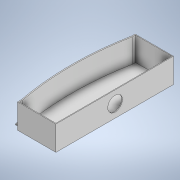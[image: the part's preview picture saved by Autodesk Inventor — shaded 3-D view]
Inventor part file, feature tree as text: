
AUTODESK INVENTOR PART (.ipt)
format: ipt  version: 2020.2 (Build 242310000, 310)  size: 199,680 bytes
history: native  units: mm
features: extrude x9, sketch x9
ambient origin geometry x8: Origin, YZ Plane, XZ Plane, XY Plane, X Axis, Y Axis, Z Axis, Center Point
bodies: Solide1 (feature_tree)
feature tree (18):
  extrude  "Extrusion1"  Depth=301.169mm
  extrude  "Extrusion2"  Depth=65.0mm TaperAngle=0.0deg
  extrude  "Extrusion3"  Depth=10.0mm TaperAngle=0.0deg
  extrude  "Extrusion4"  Depth=10.0mm TaperAngle=0.0deg
  extrude  "Extrusion5"  Depth=2.0mm
  extrude  "Extrusion6"  Depth=2.0mm
  extrude  "Extrusion7"  Depth=100.0mm TaperAngle=0.0deg
  extrude  "Extrusion8"  Depth=2.0mm TaperAngle=0.0deg
  extrude  "Extrusion9"  Depth=2.0mm TaperAngle=0.0deg
  sketch  "Esquisse1"
  sketch  "Esquisse2"
  sketch  "Esquisse3"
  sketch  "Esquisse4"
  sketch  "Esquisse5"
  sketch  "Esquisse7"
  sketch  "Esquisse8"
  sketch  "Esquisse9"
  sketch  "Esquisse10"
